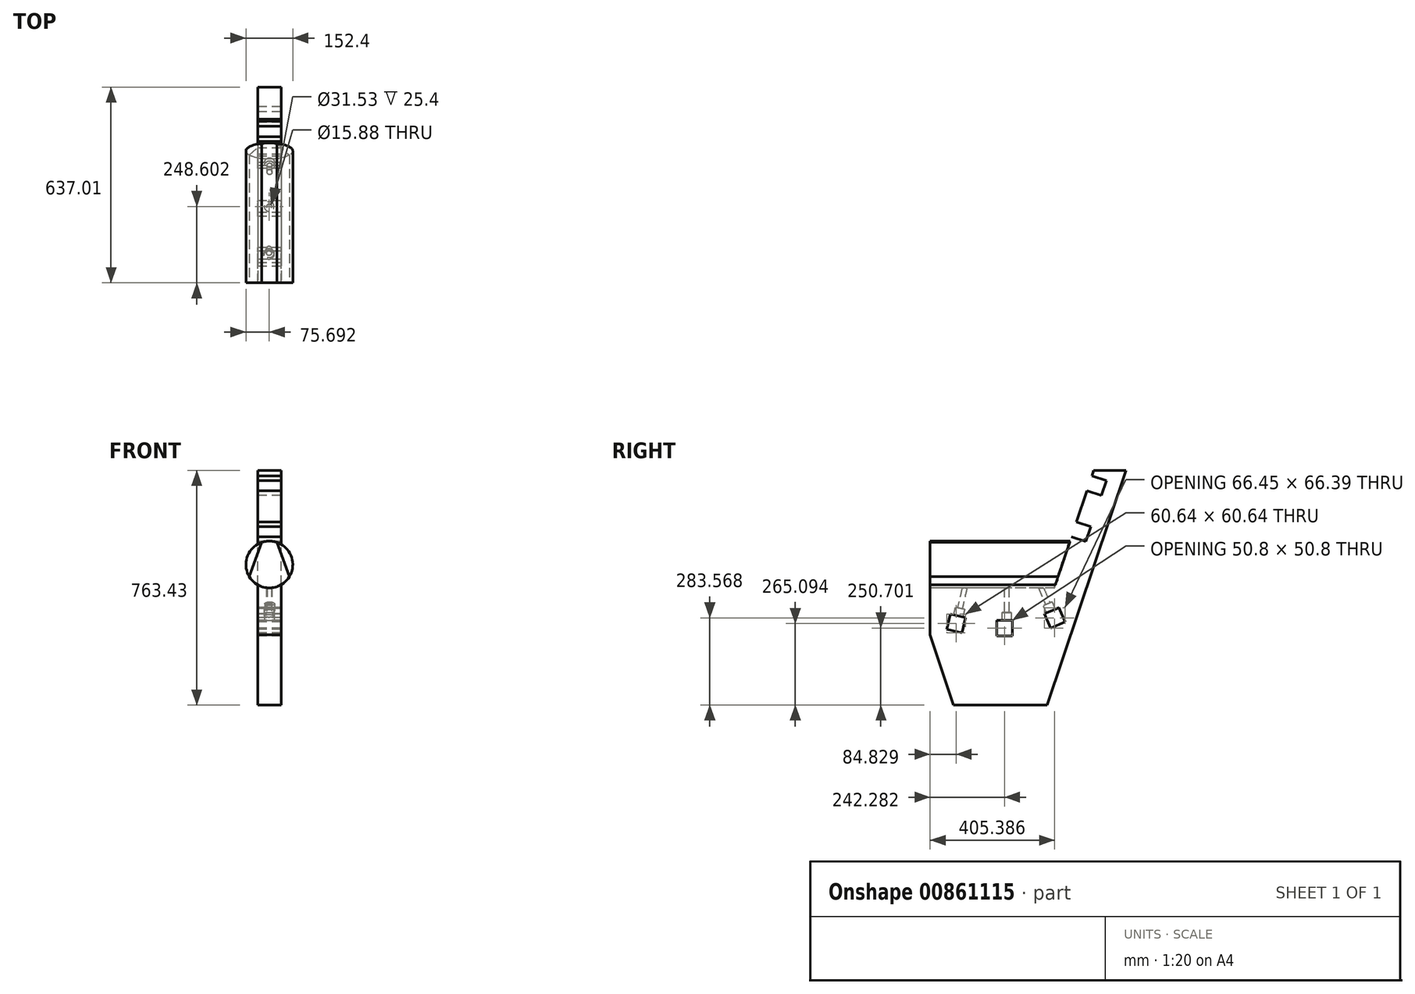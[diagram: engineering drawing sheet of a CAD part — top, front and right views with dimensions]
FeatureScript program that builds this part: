
annotation { "Feature Type Name" : "Feature", "Feature Type Description" : "" }
export const myFeature = defineFeature(function(context is Context, id is Id, definition is map)
    precondition{}
    {
        {
            var Q0;
            Q0=qCreatedBy(makeId("Right.planeOp"),FACE);
            var sketch = newSketch(context, id + "F0", { "sketchPlane" : qUnion([Q0])});
            skLineSegment(sketch, "E0.bottom", {"start": v(191.7, 94.5) * mm, "end": v(-265.5, 94.5) * mm});
            skLineSegment(sketch, "E0.top", {"start": v(191.7, -235.7) * mm, "end": v(-265.5, -235.7) * mm});
            skLineSegment(sketch, "E0.left", {"start": v(191.7, 94.5) * mm, "end": v(191.7, -235.7) * mm});
            skLineSegment(sketch, "E0.right", {"start": v(-265.5, 94.5) * mm, "end": v(-265.5, -235.7) * mm});
            skPoint(sketch, "E0.middle", {"position": v(-36.9, -70.6) * mm});
            skLineSegment(sketch, "E1", {"start": v(-265.5, -7.1) * mm, "end": v(-189.3, -235.7) * mm});
            skLineSegment(sketch, "E2", {"start": v(191.7, -8.48) * mm, "end": v(115.5, -235.7) * mm});
            skLineSegment(sketch, "E3", {"start": v(-265.5, -7.1) * mm, "end": v(191.7, -7.1) * mm, "construction": true});
            skLineSegment(sketch, "E4", {"start": v(191.7, -235.7) * mm, "end": v(191.7, 527.72) * mm});
            skLineSegment(sketch, "E5", {"start": v(10.73, -235.7) * mm, "end": v(266.75, 527.72) * mm});
            skLineSegment(sketch, "E6", {"start": v(191.7, 527.72) * mm, "end": v(266.75, 527.72) * mm, "construction": true});
            skLineSegment(sketch, "E7", {"start": v(115.5, -235.7) * mm, "end": v(371.52, 527.72) * mm});
            skLineSegment(sketch, "E8.trimOffspring", {"start": v(371.52, 527.72) * mm, "end": v(854.35, 527.72) * mm, "construction": true});
            skLineSegment(sketch, "E9", {"start": v(266.75, 527.72) * mm, "end": v(371.52, 527.72) * mm});
            skPoint(sketch, "E10", {"position": v(297.6, 527.72) * mm});
            skSolve(sketch);
        }
        {
            var Q0;
            {var subQ0=sQuery(id+"F0.wireOp",EDGE,"E1");Q0=makeQuery(id+"F0.imprint","IMPRINT",FACE,{"disambiguationData":[TD([[makeQuery(id+"F0.imprint","IMPRINT",EDGE,{"derivedFrom":subQ0}),1.0]])]});}
            var Q1;
            {var subQ3=sQuery(id+"F0.wireOp",EDGE,"E0.bottom");var subQ7=sQuery(id+"F0.wireOp",EDGE,"E4");var subQ8=makeQuery(id+"F0.imprint","INTERSECT",VERTEX,{"derivedFrom":[subQ3,subQ7]});Q1=makeQuery(id+"F0.imprint","IMPRINT",FACE,{"disambiguationData":[TD([[makeQuery(id+"F0.imprint","IMPRINT",EDGE,{"disambiguationData":[TD([[subQ8,-1.0]])],"derivedFrom":subQ3}),1.0]])]});}
            var Q2;
            {var subQ0=sQuery(id+"F0.wireOp",EDGE,"E9");Q2=makeQuery(id+"F0.imprint","IMPRINT",FACE,{"disambiguationData":[TD([[makeQuery(id+"F0.imprint","IMPRINT",EDGE,{"derivedFrom":subQ0}),-1.0]])]});}
            var Q3;
            {var subQ0=sQuery(id+"F0.wireOp",EDGE,"E4");var subQ1=sQuery(id+"F0.wireOp",EDGE,"E0.bottom");var subQ2=makeQuery(id+"F0.imprint","INTERSECT",VERTEX,{"derivedFrom":[subQ1,subQ0]});Q3=makeQuery(id+"F0.imprint","IMPRINT",FACE,{"disambiguationData":[TD([[makeQuery(id+"F0.imprint","IMPRINT",EDGE,{"disambiguationData":[TD([[subQ2,-1.0]])],"derivedFrom":subQ1}),-1.0]])]});}
            extrude(context, id + "F1", {"entities" : qUnion([Q0, Q1, Q2, Q3]), "depth" : 76.2 * mm, "offsetDistance" : 25.4 * mm});
        }
        {
            var Q0;
            Q0=makeQuery(id+"F1.opExtrude","CAP_FACE",FACE,{"disambiguationData":[OSD([sQuery(id+"F0.wireOp",EDGE,"E0.bottom"),sQuery(id+"F0.wireOp",EDGE,"E0.top"),sQuery(id+"F0.wireOp",EDGE,"E0.right"),sQuery(id+"F0.wireOp",EDGE,"E1"),sQuery(id+"F0.wireOp",EDGE,"E5"),sQuery(id+"F0.wireOp",EDGE,"E7"),sQuery(id+"F0.wireOp",EDGE,"E9")])],"isStart":true});
            var sketch = newSketch(context, id + "F2", { "sketchPlane" : qUnion([Q0])});
            skLineSegment(sketch, "E11", {"start": v(265.5, 43.7) * mm, "end": v(-209.2, 43.7) * mm, "construction": true});
            skCircle(sketch, "E12", {"center": v(186.47, 43.7) * mm, "radius": 76.2 * mm});
            skCircle(sketch, "E13", {"center": v(28.15, 43.7) * mm, "radius": 76.2 * mm});
            skCircle(sketch, "E14", {"center": v(-127.35, 43.7) * mm, "radius": 76.2 * mm});
            skLineSegment(sketch, "E15", {"start": v(-319.13, 527.72) * mm, "end": v(-92.3, -148.68) * mm, "construction": true});
            skCircle(sketch, "E16", {"center": v(-299.82, 470.11) * mm, "radius": 76.2 * mm});
            skCircle(sketch, "E17", {"center": v(-249.56, 320.24) * mm, "radius": 76.2 * mm});
            skLineSegment(sketch, "E18", {"start": v(-299.82, 470.11) * mm, "end": v(-227.57, 494.34) * mm, "construction": true});
            skLineSegment(sketch, "E19", {"start": v(-249.56, 320.24) * mm, "end": v(-177.31, 344.46) * mm, "construction": true});
            skLineSegment(sketch, "E20", {"start": v(28.15, 43.7) * mm, "end": v(28.15, 119.9) * mm, "construction": true});
            skLineSegment(sketch, "E21", {"start": v(186.47, 43.7) * mm, "end": v(186.47, 119.9) * mm, "construction": true});
            skLineSegment(sketch, "E22", {"start": v(-127.35, 43.7) * mm, "end": v(-127.35, 119.9) * mm, "construction": true});
            skLineSegment(sketch, "E23.0", {"start": v(-121.47, 94.5) * mm, "end": v(-266.75, 527.72) * mm});
            skLineSegment(sketch, "E24.bottom", {"start": v(-307.9, 494.2) * mm, "end": v(-259.73, 510.35) * mm});
            skLineSegment(sketch, "E24.top", {"start": v(-291.74, 446.03) * mm, "end": v(-243.58, 462.18) * mm});
            skLineSegment(sketch, "E24.left", {"start": v(-307.9, 494.2) * mm, "end": v(-291.74, 446.03) * mm});
            skLineSegment(sketch, "E24.right", {"start": v(-259.73, 510.35) * mm, "end": v(-243.58, 462.18) * mm});
            skLineSegment(sketch, "E25.bottom", {"start": v(-257.63, 344.32) * mm, "end": v(-209.47, 360.47) * mm});
            skLineSegment(sketch, "E25.top", {"start": v(-241.48, 296.15) * mm, "end": v(-193.32, 312.3) * mm});
            skLineSegment(sketch, "E25.left", {"start": v(-257.63, 344.32) * mm, "end": v(-241.48, 296.15) * mm});
            skLineSegment(sketch, "E25.right", {"start": v(-209.47, 360.47) * mm, "end": v(-193.32, 312.3) * mm});
            skSolve(sketch);
        }
        {
            var Q0;
            {var subQ5=sQuery(id+"F2.wireOp",EDGE,"E24.left");Q0=makeQuery(id+"F2.imprint","IMPRINT",FACE,{"disambiguationData":[TD([[makeQuery(id+"F2.imprint","IMPRINT",EDGE,{"derivedFrom":subQ5}),1.0]])]});}
            var Q1;
            {var subQ5=sQuery(id+"F2.wireOp",EDGE,"E25.left");Q1=makeQuery(id+"F2.imprint","IMPRINT",FACE,{"disambiguationData":[TD([[makeQuery(id+"F2.imprint","IMPRINT",EDGE,{"derivedFrom":subQ5}),1.0]])]});}
            extrude(context, id + "F3", {"entities" : qUnion([Q0, Q1]), "operationType" : NewBodyOperationType.REMOVE, "oppositeDirection" : true, "depth" : 76.2 * mm, "offsetDistance" : 25.4 * mm});
        }
        {
            var Q0;
            Q0=makeQuery(id+"F1.opExtrude","CAP_FACE",FACE,{"disambiguationData":[OSD([sQuery(id+"F0.wireOp",EDGE,"E0.bottom"),sQuery(id+"F0.wireOp",EDGE,"E0.top"),sQuery(id+"F0.wireOp",EDGE,"E0.right"),sQuery(id+"F0.wireOp",EDGE,"E1"),sQuery(id+"F0.wireOp",EDGE,"E5"),sQuery(id+"F0.wireOp",EDGE,"E7"),sQuery(id+"F0.wireOp",EDGE,"E9")])],"isStart":true});
            var sketch = newSketch(context, id + "F4", { "sketchPlane" : qUnion([Q0])});
            skCircle(sketch, "E26", {"center": v(177.67, 55.38) * mm, "radius": 76.2 * mm});
            skCircle(sketch, "E27", {"center": v(-127.45, 70.99) * mm, "radius": 76.2 * mm});
            skCircle(sketch, "E28", {"center": v(23.4, 40.9) * mm, "radius": 76.2 * mm});
            skCircle(sketch, "E29", {"center": v(51.22, 573.57) * mm, "radius": 533.4 * mm});
            skLineSegment(sketch, "E30", {"start": v(-236.22, 124.25) * mm, "end": v(265.5, 124.25) * mm, "construction": true});
            skLineSegment(sketch, "E31", {"start": v(23.4, 40.9) * mm, "end": v(23.4, -35.3) * mm, "construction": true});
            skLineSegment(sketch, "E32", {"start": v(177.67, 55.38) * mm, "end": v(195.93, -18.6) * mm, "construction": true});
            skLineSegment(sketch, "E33", {"start": v(-127.45, 70.99) * mm, "end": v(-159.92, 2.05) * mm, "construction": true});
            skLineSegment(sketch, "E34.bottom", {"start": v(-126.24, 14.66) * mm, "end": v(-173.12, 34.23) * mm});
            skLineSegment(sketch, "E34.top", {"start": v(-106.67, 61.54) * mm, "end": v(-153.55, 81.1) * mm});
            skLineSegment(sketch, "E34.left", {"start": v(-126.24, 14.66) * mm, "end": v(-106.67, 61.54) * mm});
            skLineSegment(sketch, "E34.right", {"start": v(-173.12, 34.23) * mm, "end": v(-153.55, 81.1) * mm});
            skPoint(sketch, "E34.middle", {"position": v(-139.9, 47.88) * mm});
            skLineSegment(sketch, "E35.bottom", {"start": v(48.6, -10.4) * mm, "end": v(-2.2, -10.4) * mm});
            skLineSegment(sketch, "E35.top", {"start": v(48.6, 40.4) * mm, "end": v(-2.2, 40.4) * mm});
            skLineSegment(sketch, "E35.left", {"start": v(48.6, -10.4) * mm, "end": v(48.6, 40.4) * mm});
            skLineSegment(sketch, "E35.right", {"start": v(-2.2, -10.4) * mm, "end": v(-2.2, 40.4) * mm});
            skPoint(sketch, "E35.middle", {"position": v(23.2, 15) * mm});
            skLineSegment(sketch, "E36.bottom", {"start": v(210.98, 10.13) * mm, "end": v(161.4, -0.94) * mm});
            skLineSegment(sketch, "E36.top", {"start": v(199.92, 59.7) * mm, "end": v(150.34, 48.64) * mm});
            skLineSegment(sketch, "E36.left", {"start": v(210.98, 10.13) * mm, "end": v(199.92, 59.7) * mm});
            skLineSegment(sketch, "E36.right", {"start": v(161.4, -0.94) * mm, "end": v(150.34, 48.64) * mm});
            skPoint(sketch, "E36.middle", {"position": v(180.66, 29.38) * mm});
            skSolve(sketch);
        }
        {
            var Q0;
            {var subQ6=sQuery(id+"F4.wireOp",EDGE,"E34.bottom");Q0=makeQuery(id+"F4.imprint","IMPRINT",FACE,{"disambiguationData":[TD([[makeQuery(id+"F4.imprint","IMPRINT",EDGE,{"derivedFrom":subQ6}),-1.0]])]});}
            var Q1;
            {var subQ4=sQuery(id+"F4.wireOp",EDGE,"E35.bottom");Q1=makeQuery(id+"F4.imprint","IMPRINT",FACE,{"disambiguationData":[TD([[makeQuery(id+"F4.imprint","IMPRINT",EDGE,{"derivedFrom":subQ4}),-1.0]])]});}
            var Q2;
            Q2=makeQuery(id+"F4.imprint","IMPRINT",FACE,{"disambiguationData":[TD([[makeQuery(id+"F4.imprint","IMPRINT",EDGE,{"derivedFrom":sQuery(id+"F4.wireOp",EDGE,"E36.bottom")}),-1.0]])]});
            extrude(context, id + "F5", {"entities" : qUnion([Q0, Q1, Q2]), "operationType" : NewBodyOperationType.REMOVE, "oppositeDirection" : true, "depth" : 76.2 * mm, "offsetDistance" : 25.4 * mm});
        }
        {
            var Q0;
            Q0=makeQuery(id+"F1.opExtrude","SWEPT_FACE",FACE,{"disambiguationData":[OSD([sQuery(id+"F0.wireOp",EDGE,"E0.right")])]});
            var sketch = newSketch(context, id + "F6", { "sketchPlane" : qUnion([Q0])});
            skLineSegment(sketch, "E37", {"start": v(38.1, 94.5) * mm, "end": v(38.1, 297.7) * mm, "construction": true});
            skCircle(sketch, "E38", {"center": v(38.1, 221.5) * mm, "radius": 76.2 * mm});
            skPoint(sketch, "E39", {"position": v(76.2, 155.5) * mm});
            skLineSegment(sketch, "E40.bottom", {"start": v(0, 94.5) * mm, "end": v(76.2, 94.5) * mm});
            skLineSegment(sketch, "E40.top", {"start": v(0, 155.5) * mm, "end": v(76.2, 155.5) * mm});
            skLineSegment(sketch, "E40.left", {"start": v(0, 94.5) * mm, "end": v(0, 155.5) * mm});
            skLineSegment(sketch, "E40.right", {"start": v(76.2, 94.5) * mm, "end": v(76.2, 155.5) * mm});
            skSolve(sketch);
        }
        {
            var Q0;
            Q0=makeQuery(id+"F6.imprint","IMPRINT",FACE,{"disambiguationData":[TD([[makeQuery(id+"F6.imprint","IMPRINT",EDGE,{"derivedFrom":sQuery(id+"F6.wireOp",EDGE,"E40.bottom")}),-1.0]])]});
            extrude(context, id + "F7", {"entities" : qUnion([Q0]), "operationType" : NewBodyOperationType.ADD, "oppositeDirection" : true, "depth" : 417.83 * mm, "offsetDistance" : 25.4 * mm});
        }
        {
            var Q0;
            Q0=makeQuery(id+"F7.opExtrude","SWEPT_FACE",FACE,{"disambiguationData":[OSD([sQuery(id+"F6.wireOp",EDGE,"E40.right")])]});
            var Q1;
            Q1=makeQuery(id+"F1.opExtrude","CAP_FACE",FACE,{"disambiguationData":[OSD([sQuery(id+"F0.wireOp",EDGE,"E0.bottom"),sQuery(id+"F0.wireOp",EDGE,"E0.top"),sQuery(id+"F0.wireOp",EDGE,"E0.right"),sQuery(id+"F0.wireOp",EDGE,"E1"),sQuery(id+"F0.wireOp",EDGE,"E5"),sQuery(id+"F0.wireOp",EDGE,"E7"),sQuery(id+"F0.wireOp",EDGE,"E9")])],"isStart":false});
            extrude(context, id + "F8", {"entities" : qUnion([Q0]), "operationType" : NewBodyOperationType.ADD, "endBound" : BoundingType.UP_TO_SURFACE, "depth" : 25.4 * mm, "endBoundEntityFace" : qUnion([Q1]), "offsetDistance" : 25.4 * mm});
        }
        {
            var Q0;
            Q0=makeQuery(id+"F5.boolean.opBoolean","COPY",FACE,{"derivedFrom":makeQuery(id+"F5.opExtrude","SWEPT_FACE",FACE,{"disambiguationData":[OSD([sQuery(id+"F4.wireOp",EDGE,"E36.top")])]})});
            var sketch = newSketch(context, id + "F9", { "sketchPlane" : qUnion([Q0])});
            skCircle(sketch, "E41", {"center": v(36.97, 181.73) * mm, "radius": 15.76 * mm});
            skSolve(sketch);
        }
        {
            var Q0;
            Q0=makeQuery(id+"F5.boolean.opBoolean","COPY",FACE,{"derivedFrom":makeQuery(id+"F5.opExtrude","SWEPT_FACE",FACE,{"disambiguationData":[OSD([sQuery(id+"F4.wireOp",EDGE,"E35.top")])]})});
            var sketch = newSketch(context, id + "F10", { "sketchPlane" : qUnion([Q0])});
            skCircle(sketch, "E42", {"center": v(37.6, 16.89) * mm, "radius": 15.76 * mm});
            skPoint(sketch, "E43", {"position": v(76.2, 16.89) * mm});
            skSolve(sketch);
        }
        {
            var Q0;
            Q0=makeQuery(id+"F5.boolean.opBoolean","COPY",FACE,{"derivedFrom":makeQuery(id+"F5.opExtrude","SWEPT_FACE",FACE,{"disambiguationData":[OSD([sQuery(id+"F4.wireOp",EDGE,"E34.top")])]})});
            var sketch = newSketch(context, id + "F11", { "sketchPlane" : qUnion([Q0])});
            skCircle(sketch, "E44", {"center": v(38.89, -144.18) * mm, "radius": 15.76 * mm});
            skSolve(sketch);
        }
        {
            var Q0;
            Q0=makeQuery(id+"F9.imprint","IMPRINT",FACE,{"disambiguationData":[TD([[makeQuery(id+"F9.imprint","IMPRINT",EDGE,{"derivedFrom":sQuery(id+"F9.wireOp",EDGE,"E41")}),1.0]])]});
            var Q1;
            Q1=sQuery(id+"F9.wireOp",EDGE,"E41");
            extrude(context, id + "F12", {"entities" : qUnion([Q0]), "operationType" : NewBodyOperationType.REMOVE, "surfaceEntities" : qUnion([Q1]), "oppositeDirection" : true, "depth" : 25.4 * mm, "offsetDistance" : 25.4 * mm});
        }
        {
            var Q0;
            Q0=makeQuery(id+"F10.imprint","IMPRINT",FACE,{"disambiguationData":[TD([[makeQuery(id+"F10.imprint","IMPRINT",EDGE,{"derivedFrom":sQuery(id+"F10.wireOp",EDGE,"E42")}),1.0]])]});
            extrude(context, id + "F13", {"entities" : qUnion([Q0]), "operationType" : NewBodyOperationType.REMOVE, "oppositeDirection" : true, "depth" : 25.4 * mm, "offsetDistance" : 25.4 * mm});
        }
        {
            var Q0;
            Q0=makeQuery(id+"F11.imprint","IMPRINT",FACE,{"disambiguationData":[TD([[makeQuery(id+"F11.imprint","IMPRINT",EDGE,{"derivedFrom":sQuery(id+"F11.wireOp",EDGE,"E44")}),1.0]])]});
            extrude(context, id + "F14", {"entities" : qUnion([Q0]), "operationType" : NewBodyOperationType.REMOVE, "oppositeDirection" : true, "depth" : 25.4 * mm, "offsetDistance" : 25.4 * mm});
        }
        {
            var Q0;
            Q0=makeQuery(id+"F12.boolean.opBoolean","COPY",FACE,{"derivedFrom":makeQuery(id+"F12.opExtrude","CAP_FACE",FACE,{"disambiguationData":[OSD([sQuery(id+"F9.wireOp",EDGE,"E41")])],"isStart":false})});
            var sketch = newSketch(context, id + "F15", { "sketchPlane" : qUnion([Q0])});
            skCircle(sketch, "E45", {"center": v(36.97, 181.73) * mm, "radius": 7.94 * mm});
            skSolve(sketch);
        }
        {
            var Q0;
            Q0=makeQuery(id+"F13.boolean.opBoolean","COPY",FACE,{"derivedFrom":makeQuery(id+"F13.opExtrude","CAP_FACE",FACE,{"disambiguationData":[OSD([sQuery(id+"F10.wireOp",EDGE,"E42")])],"isStart":false})});
            var sketch = newSketch(context, id + "F16", { "sketchPlane" : qUnion([Q0])});
            skCircle(sketch, "E46", {"center": v(37.6, 16.89) * mm, "radius": 7.94 * mm});
            skSolve(sketch);
        }
        {
            var Q0;
            Q0=makeQuery(id+"F14.boolean.opBoolean","COPY",FACE,{"derivedFrom":makeQuery(id+"F14.opExtrude","CAP_FACE",FACE,{"disambiguationData":[OSD([sQuery(id+"F11.wireOp",EDGE,"E44")])],"isStart":false})});
            var sketch = newSketch(context, id + "F17", { "sketchPlane" : qUnion([Q0])});
            skCircle(sketch, "E47", {"center": v(38.89, -144.18) * mm, "radius": 7.94 * mm});
            skSolve(sketch);
        }
        {
            var Q0;
            Q0=makeQuery(id+"F17.imprint","IMPRINT",FACE,{"disambiguationData":[TD([[makeQuery(id+"F17.imprint","IMPRINT",EDGE,{"derivedFrom":sQuery(id+"F17.wireOp",EDGE,"E47")}),1.0]])]});
            extrude(context, id + "F18", {"entities" : qUnion([Q0]), "operationType" : NewBodyOperationType.REMOVE, "oppositeDirection" : true, "depth" : 78.74 * mm, "offsetDistance" : 25.4 * mm});
        }
        {
            var Q0;
            Q0=makeQuery(id+"F16.imprint","IMPRINT",FACE,{"disambiguationData":[TD([[makeQuery(id+"F16.imprint","IMPRINT",EDGE,{"derivedFrom":sQuery(id+"F16.wireOp",EDGE,"E46")}),1.0]])]});
            var Q1;
            Q1=sQuery(id+"F16.wireOp",EDGE,"E46");
            extrude(context, id + "F19", {"entities" : qUnion([Q0]), "operationType" : NewBodyOperationType.REMOVE, "surfaceEntities" : qUnion([Q1]), "oppositeDirection" : true, "depth" : 111.25 * mm, "offsetDistance" : 25.4 * mm});
        }
        {
            var Q0;
            Q0=makeQuery(id+"F15.imprint","IMPRINT",FACE,{"disambiguationData":[TD([[makeQuery(id+"F15.imprint","IMPRINT",EDGE,{"derivedFrom":sQuery(id+"F15.wireOp",EDGE,"E45")}),1.0]])]});
            var Q1;
            Q1=sQuery(id+"F15.wireOp",EDGE,"E45");
            extrude(context, id + "F20", {"entities" : qUnion([Q0]), "operationType" : NewBodyOperationType.REMOVE, "surfaceEntities" : qUnion([Q1]), "oppositeDirection" : true, "depth" : 90.42 * mm, "offsetDistance" : 25.4 * mm});
        }
        {
            var Q0;
            Q0=makeQuery(id+"F7.boolean.opBoolean","MERGE",FACE,{"derivedFrom":[makeQuery(id+"F1.opExtrude","SWEPT_FACE",FACE,{"disambiguationData":[OSD([sQuery(id+"F0.wireOp",EDGE,"E0.right")])]}),makeQuery(id+"F7.opExtrude","CAP_FACE",FACE,{"disambiguationData":[OSD([sQuery(id+"F6.wireOp",EDGE,"E38"),sQuery(id+"F6.wireOp",EDGE,"E40.bottom"),sQuery(id+"F6.wireOp",EDGE,"E40.left"),sQuery(id+"F6.wireOp",EDGE,"E40.right")])],"isStart":true})]});
            var sketch = newSketch(context, id + "F21", { "sketchPlane" : qUnion([Q0])});
            skLineSegment(sketch, "E48", {"start": v(38.1, -7.1) * mm, "end": v(38.1, 437.64) * mm, "construction": true});
            skPoint(sketch, "E49", {"position": v(38.1, 221.5) * mm});
            skPoint(sketch, "E50", {"position": v(38.1, 145.3) * mm});
            skCircle(sketch, "E51", {"center": v(38.1, 221.5) * mm, "radius": 76.2 * mm});
            skSolve(sketch);
        }
        {
            var Q0;
            {var subQ0=sQuery(id+"F21.wireOp",EDGE,"E51");var subQ2=makeQuery(id+"F21.imprint","INTERSECT",VERTEX,{"derivedFrom":[makeQuery(id+"F7.opExtrude","CAP_EDGE",EDGE,{"disambiguationData":[OSD([sQuery(id+"F6.wireOp",EDGE,"E40.right")])],"isStart":true}),subQ0]});Q0=makeQuery(id+"F21.imprint","IMPRINT",FACE,{"disambiguationData":[TD([[makeQuery(id+"F21.imprint","IMPRINT",EDGE,{"disambiguationData":[TD([[subQ2,1.0]])],"derivedFrom":subQ0}),1.0]])]});}
            var Q1;
            {var subQ0=sQuery(id+"F0.wireOp",EDGE,"E0.bottom");var subQ3=sQuery(id+"F0.wireOp",EDGE,"E5");Q1=makeQuery(id+"F3.boolean.opBoolean","SPLIT",FACE,{"disambiguationData":[TD([makeQuery(id+"F1.opExtrude","SWEPT_FACE",FACE,{"disambiguationData":[OSD([subQ0])]})])],"derivedFrom":makeQuery(id+"F1.opExtrude","SWEPT_FACE",FACE,{"disambiguationData":[OSD([subQ3])]})});}
            extrude(context, id + "F22", {"entities" : qUnion([Q0]), "endBound" : BoundingType.UP_TO_SURFACE, "oppositeDirection" : true, "depth" : 475.23 * mm, "endBoundEntityFace" : qUnion([Q1]), "offsetDistance" : 25.4 * mm});
        }
        {
            var Q0;
            Q0=makeQuery(id+"F22.opExtrude","CAP_FACE",FACE,{"disambiguationData":[OSD([sQuery(id+"F21.wireOp",EDGE,"E51")])],"isStart":true});
            var sketch = newSketch(context, id + "F23", { "sketchPlane" : qUnion([Q0])});
            skLineSegment(sketch, "E52", {"start": v(13.8, 293.71) * mm, "end": v(-27.1, 182.06) * mm});
            skSolve(sketch);
        }
        {
            var Q0;
            {var subQ0=sQuery(id+"F23.wireOp",EDGE,"E52");Q0=makeQuery(id+"F23.imprint","IMPRINT",FACE,{"disambiguationData":[TD([[makeQuery(id+"F23.imprint","IMPRINT",EDGE,{"derivedFrom":subQ0}),-1.0]])]});}
            extrude(context, id + "F24", {"entities" : qUnion([Q0]), "operationType" : NewBodyOperationType.REMOVE, "endBound" : BoundingType.UP_TO_NEXT, "oppositeDirection" : true, "depth" : 390.9 * mm, "offsetDistance" : 25.4 * mm});
        }
        {
            var Q0;
            Q0=makeQuery(id+"F22.opExtrude","CAP_FACE",FACE,{"disambiguationData":[OSD([sQuery(id+"F21.wireOp",EDGE,"E51")])],"isStart":true});
            var sketch = newSketch(context, id + "F25", { "sketchPlane" : qUnion([Q0])});
            skCircle(sketch, "E53", {"center": v(38.1, 221.5) * mm, "radius": 76.2 * mm});
            skLineSegment(sketch, "E54", {"start": v(38.1, 221.5) * mm, "end": v(38.1, 297.7) * mm, "construction": true});
            skLineSegment(sketch, "E55", {"start": v(-27.1, 182.06) * mm, "end": v(13.8, 293.71) * mm});
            skLineSegment(sketch, "E56.MirrorCS", {"start": v(103.3, 182.06) * mm, "end": v(62.4, 293.71) * mm});
            skSolve(sketch);
        }
        {
            var Q0;
            {var subQ0=sQuery(id+"F25.wireOp",EDGE,"E55");Q0=makeQuery(id+"F25.imprint","IMPRINT",FACE,{"disambiguationData":[TD([[makeQuery(id+"F25.imprint","IMPRINT",EDGE,{"derivedFrom":subQ0}),1.0]])]});}
            var Q1;
            {var subQ0=sQuery(id+"F25.wireOp",EDGE,"E55");Q1=makeQuery(id+"F25.imprint","IMPRINT",FACE,{"disambiguationData":[TD([[makeQuery(id+"F25.imprint","IMPRINT",EDGE,{"derivedFrom":subQ0}),-1.0]])]});}
            var Q2;
            {var subQ0=sQuery(id+"F0.wireOp",EDGE,"E0.bottom");var subQ3=sQuery(id+"F0.wireOp",EDGE,"E5");Q2=makeQuery(id+"F3.boolean.opBoolean","SPLIT",FACE,{"disambiguationData":[TD([makeQuery(id+"F1.opExtrude","SWEPT_FACE",FACE,{"disambiguationData":[OSD([subQ0])]})])],"derivedFrom":makeQuery(id+"F1.opExtrude","SWEPT_FACE",FACE,{"disambiguationData":[OSD([subQ3])]})});}
            extrude(context, id + "F26", {"entities" : qUnion([Q0, Q1]), "endBound" : BoundingType.UP_TO_SURFACE, "oppositeDirection" : true, "depth" : 25.4 * mm, "endBoundEntityFace" : qUnion([Q2]), "offsetDistance" : 25.4 * mm});
        }
    });
